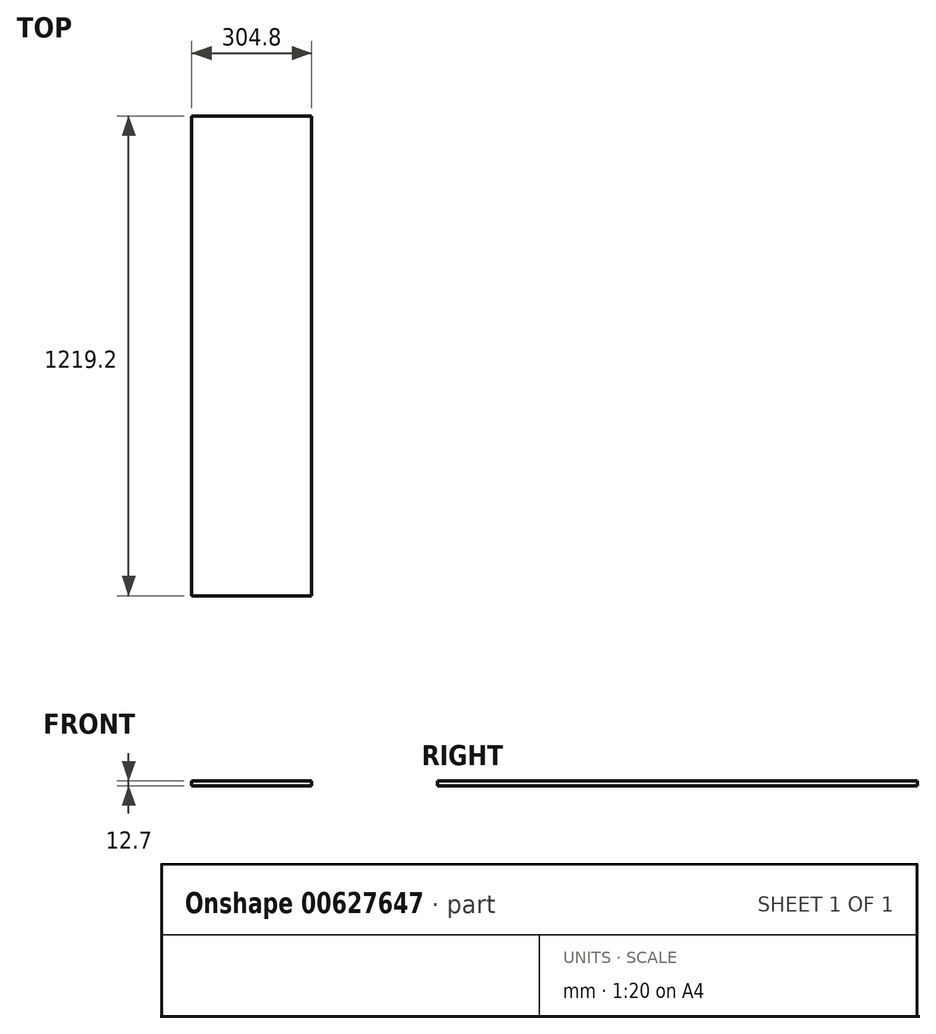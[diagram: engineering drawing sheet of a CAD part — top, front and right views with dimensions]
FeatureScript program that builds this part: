
annotation { "Feature Type Name" : "Feature", "Feature Type Description" : "" }
export const myFeature = defineFeature(function(context is Context, id is Id, definition is map)
    precondition{}
    {
        {
            var Q0;
            Q0=qCreatedBy(makeId("Top.planeOp"),FACE);
            var sketch = newSketch(context, id + "F0", { "sketchPlane" : qUnion([Q0])});
            skLineSegment(sketch, "E0.bottom", {"start": v(-152.4, 609.6) * mm, "end": v(152.4, 609.6) * mm});
            skLineSegment(sketch, "E0.top", {"start": v(-152.4, -609.6) * mm, "end": v(152.4, -609.6) * mm});
            skLineSegment(sketch, "E0.left", {"start": v(-152.4, 609.6) * mm, "end": v(-152.4, -609.6) * mm});
            skLineSegment(sketch, "E0.right", {"start": v(152.4, 609.6) * mm, "end": v(152.4, -609.6) * mm});
            skPoint(sketch, "E0.middle", {"position": v(0, 0) * mm});
            skSolve(sketch);
        }
        {
            var Q0;
            Q0 = qSketchRegion(id + "F0", true);
            extrude(context, id + "F1", {"entities" : qUnion([Q0]), "depth" : 12.7 * mm, "offsetDistance" : 25.4 * mm});
        }
    });
